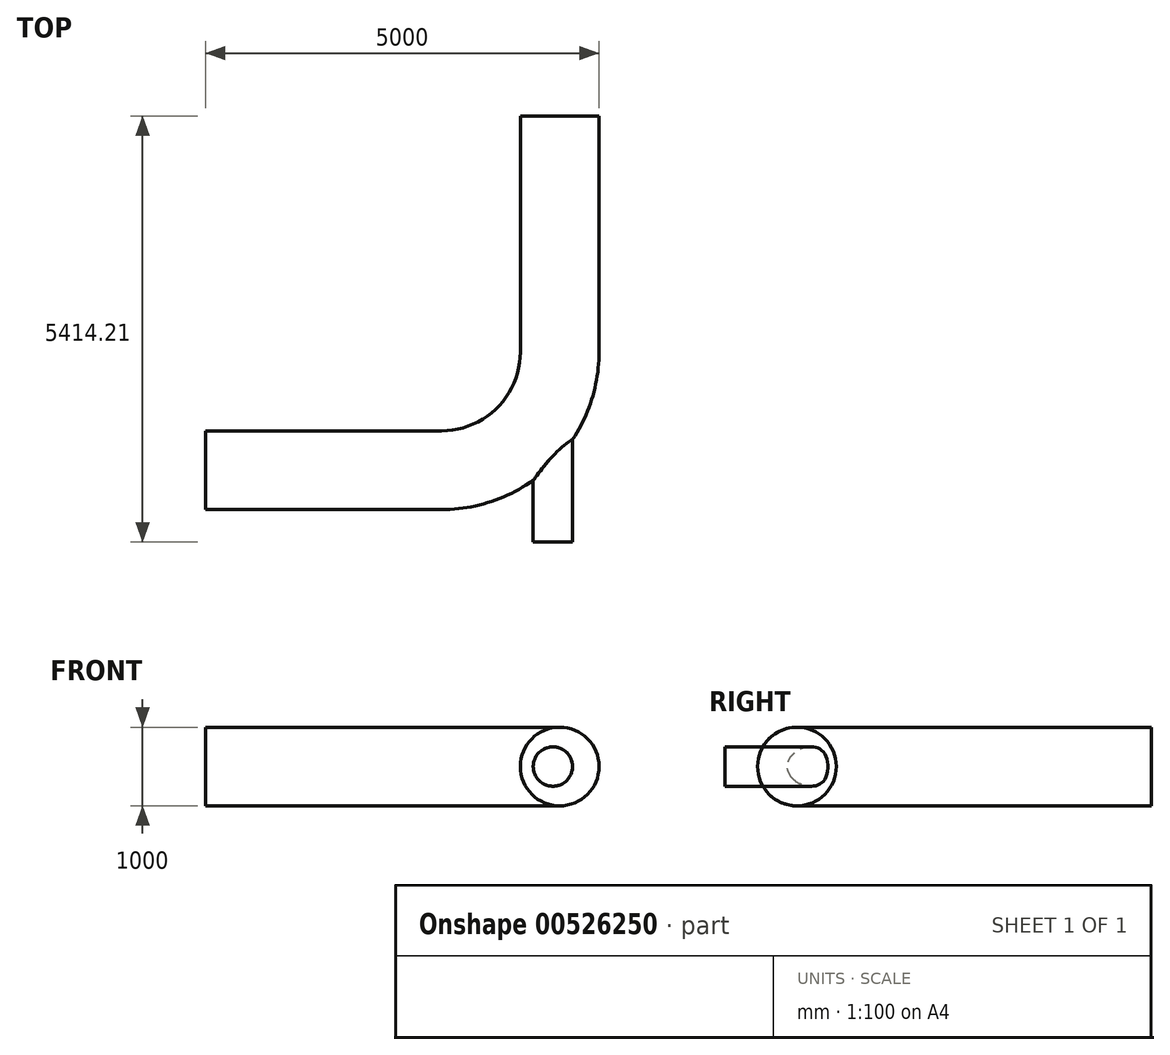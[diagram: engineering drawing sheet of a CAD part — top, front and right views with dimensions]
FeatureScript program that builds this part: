
annotation { "Feature Type Name" : "Feature", "Feature Type Description" : "" }
export const myFeature = defineFeature(function(context is Context, id is Id, definition is map)
    precondition{}
    {
        {
            var Q0;
            Q0=qCreatedBy(makeId("Top.planeOp"),FACE);
            var sketch = newSketch(context, id + "F0", { "sketchPlane" : qUnion([Q0])});
            skLineSegment(sketch, "E0", {"start": v(0, 0) * mm, "end": v(3000, 0) * mm});
            skArc(sketch, "E1", {"start": v(3000, 0) * mm, "mid": v(4060.66, 439.34) * mm, "end": v(4500, 1500) * mm});
            skLineSegment(sketch, "E2", {"start": v(4500, 1500) * mm, "end": v(4500, 4500) * mm});
            skArc(sketch, "E3.0", {"start": v(3000, -500) * mm, "mid": v(4414.21, 85.79) * mm, "end": v(5000, 1500) * mm});
            skLineSegment(sketch, "E4", {"start": v(3000, 1500) * mm, "end": v(4414.21, 85.79) * mm});
            skLineSegment(sketch, "E5", {"start": v(4414.21, 85.79) * mm, "end": v(4414.21, -914.21) * mm});
            skSolve(sketch);
        }
        {
            var Q0;
            Q0=qCreatedBy(makeId("Right.planeOp"),FACE);
            var sketch = newSketch(context, id + "F1", { "sketchPlane" : qUnion([Q0])});
            skCircle(sketch, "E6", {"center": v(0, 0) * mm, "radius": 500 * mm});
            skSolve(sketch);
        }
        {
            var Q0;
            Q0=makeQuery(id+"F1.imprint","IMPRINT",FACE,{"disambiguationData":[TD([[makeQuery(id+"F1.imprint","IMPRINT",EDGE,{"derivedFrom":sQuery(id+"F1.wireOp",EDGE,"E6")}),1.0]])]});
            var Q1;
            Q1=sQuery(id+"F0.wireOp",EDGE,"E0");
            var Q2;
            Q2=sQuery(id+"F0.wireOp",EDGE,"E1");
            var Q3;
            Q3=sQuery(id+"F0.wireOp",EDGE,"E2");
            sweep(context, id + "F2", {"profiles" : qUnion([Q0]), "path" : qUnion([Q1, Q2, Q3])});
        }
        {
            var Q0;
            Q0=sQuery(id+"F0.wireOp",VERTEX,"E5.end");
            var Q1;
            Q1=sQuery(id+"F0.wireOp",EDGE,"E5");
            cPlane(context, id + "F3", {"entities" : qUnion([Q0, Q1]), "cplaneType" : CPlaneType.LINE_POINT, "offset" : 25 * mm, "width" : 150 * mm, "height" : 150 * mm});
        }
        {
            var Q0;
            Q0=qCreatedBy(id+"F3.planeOp",FACE);
            var sketch = newSketch(context, id + "F4", { "sketchPlane" : qUnion([Q0])});
            skPoint(sketch, "E7.0", {"position": v(4414.21, 0) * mm});
            skCircle(sketch, "E8", {"center": v(4414.21, 0) * mm, "radius": 250 * mm});
            skSolve(sketch);
        }
        {
            var Q0;
            Q0=makeQuery(id+"F4.imprint","IMPRINT",FACE,{"disambiguationData":[TD([[makeQuery(id+"F4.imprint","IMPRINT",EDGE,{"derivedFrom":sQuery(id+"F4.wireOp",EDGE,"E8")}),1.0]])]});
            var Q1;
            Q1=makeQuery(id+"F2.opSweep","CAP_FACE",FACE,{"disambiguationData":[OSD([sQuery(id+"F0.wireOp",VERTEX,"E2.end"),sQuery(id+"F1.wireOp",EDGE,"E6")])],"isStart":false});
            extrude(context, id + "F5", {"entities" : qUnion([Q0]), "operationType" : NewBodyOperationType.ADD, "endBound" : BoundingType.UP_TO_SURFACE, "oppositeDirection" : true, "depth" : 1760 * mm, "endBoundEntityFace" : qUnion([Q1]), "offsetDistance" : 25 * mm});
        }
    });
